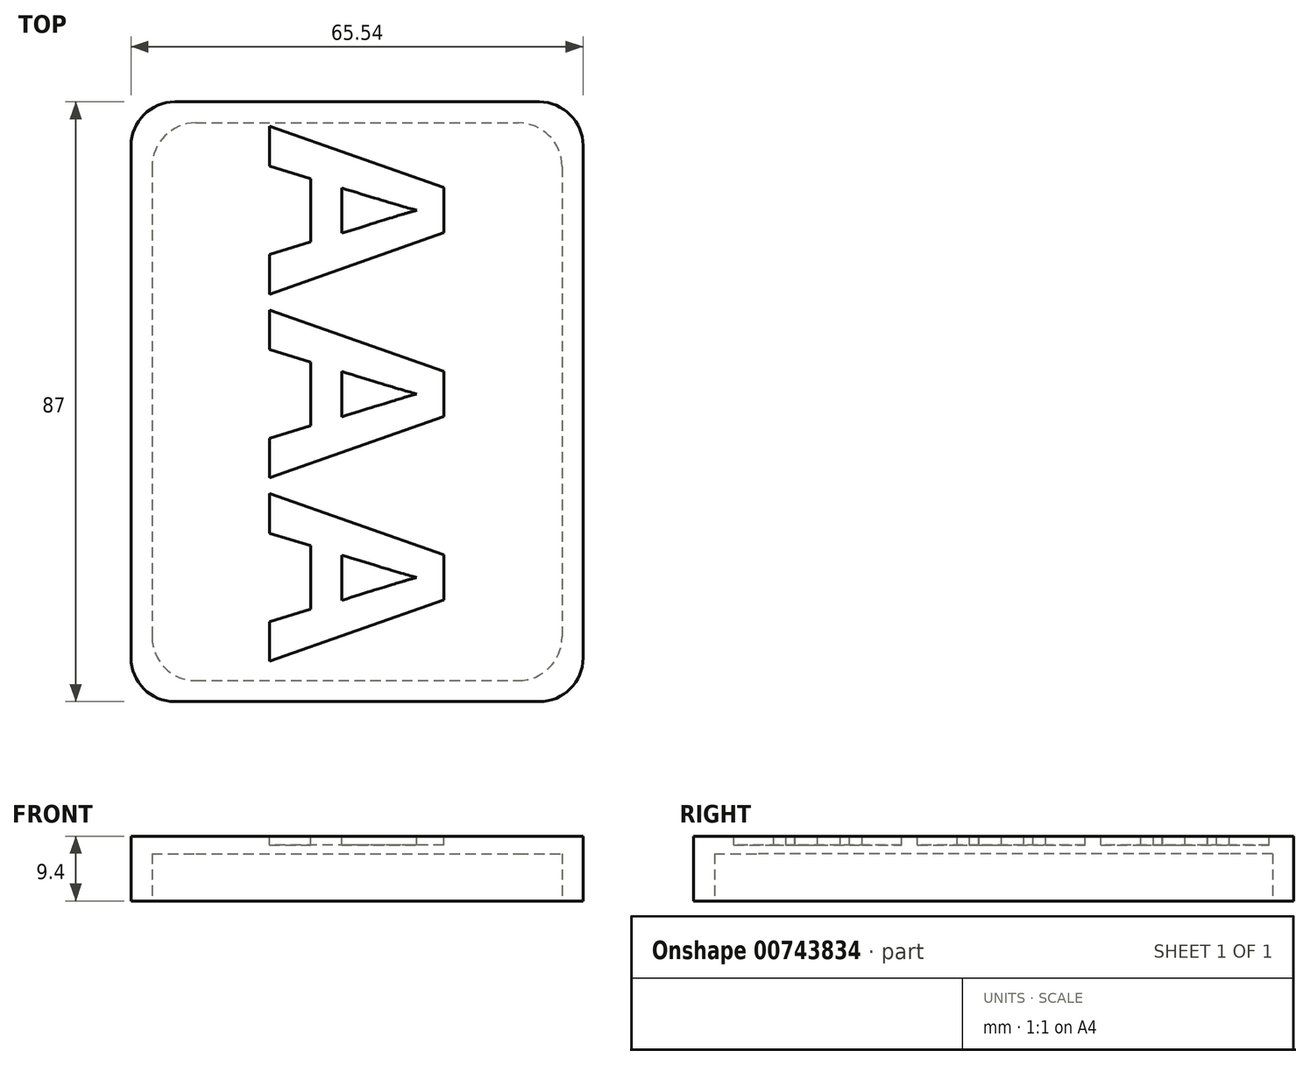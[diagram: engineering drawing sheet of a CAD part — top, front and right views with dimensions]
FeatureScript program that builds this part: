
annotation { "Feature Type Name" : "Feature", "Feature Type Description" : "" }
export const myFeature = defineFeature(function(context is Context, id is Id, definition is map)
    precondition{}
    {
        {
            var Q0;
            Q0=qCreatedBy(makeId("Top.planeOp"),FACE);
            var sketch = newSketch(context, id + "F0", { "sketchPlane" : qUnion([Q0])});
            skLineSegment(sketch, "E0.bottom", {"start": v(-32.77, 43.5) * mm, "end": v(32.77, 43.5) * mm});
            skLineSegment(sketch, "E0.top", {"start": v(-32.77, -43.5) * mm, "end": v(32.77, -43.5) * mm});
            skLineSegment(sketch, "E0.left", {"start": v(-32.77, 43.5) * mm, "end": v(-32.77, -43.5) * mm});
            skLineSegment(sketch, "E0.right", {"start": v(32.77, 43.5) * mm, "end": v(32.77, -43.5) * mm});
            skLineSegment(sketch, "E1", {"start": v(0, 43.5) * mm, "end": v(0, 0) * mm, "construction": true});
            skLineSegment(sketch, "E2", {"start": v(0, 0) * mm, "end": v(-32.77, 0) * mm, "construction": true});
            skSolve(sketch);
        }
        {
            var Q0;
            Q0=qSketchRegion(id+"F0",true);
            extrude(context, id + "F1", {"entities" : qUnion([Q0]), "depth" : 41.27 * mm, "offsetDistance" : 25.4 * mm});
        }
        {
            var Q0;
            Q0=makeQuery(id+"F1.opExtrude","CAP_FACE",FACE,{"disambiguationData":[OSD([sQuery(id+"F0.wireOp",EDGE,"E0.bottom"),sQuery(id+"F0.wireOp",EDGE,"E0.top"),sQuery(id+"F0.wireOp",EDGE,"E0.left"),sQuery(id+"F0.wireOp",EDGE,"E0.right")])],"isStart":false});
            var sketch = newSketch(context, id + "F2", { "sketchPlane" : qUnion([Q0])});
            skCircle(sketch, "E3", {"center": v(-24.2, 34.92) * mm, "radius": 5.4 * mm});
            skCircle(sketch, "E4.1.0.0", {"center": v(-24.2, 20.95) * mm, "radius": 5.4 * mm});
            skCircle(sketch, "E4.2.0.0", {"center": v(-24.2, 6.98) * mm, "radius": 5.4 * mm});
            skLineSegment(sketch, "E4.direction1", {"start": v(-24.2, 34.92) * mm, "end": v(-24.2, 20.95) * mm, "construction": true});
            skCircle(sketch, "E5.0.3.0", {"center": v(-24.2, -6.99) * mm, "radius": 5.4 * mm});
            skCircle(sketch, "E5.0.4.0", {"center": v(-24.2, -20.96) * mm, "radius": 5.4 * mm});
            skCircle(sketch, "E6.0.5.0", {"center": v(-24.2, -34.93) * mm, "radius": 5.4 * mm});
            skCircle(sketch, "E7", {"center": v(-12.1, 27.94) * mm, "radius": 5.4 * mm});
            skLineSegment(sketch, "E8", {"start": v(-12.1, 27.94) * mm, "end": v(-24.2, 34.93) * mm, "construction": true});
            skLineSegment(sketch, "E9", {"start": v(-24.2, 20.95) * mm, "end": v(-12.1, 27.94) * mm, "construction": true});
            skCircle(sketch, "E10.1.0.0", {"center": v(-12.1, 13.97) * mm, "radius": 5.4 * mm});
            skCircle(sketch, "E10.2.0.0", {"center": v(-12.1, 0) * mm, "radius": 5.4 * mm});
            skLineSegment(sketch, "E10.direction1", {"start": v(-12.1, 27.94) * mm, "end": v(-12.1, 13.97) * mm, "construction": true});
            skCircle(sketch, "E11.0.3.0", {"center": v(-12.1, -13.97) * mm, "radius": 5.4 * mm});
            skCircle(sketch, "E11.0.4.0", {"center": v(-12.1, -27.94) * mm, "radius": 5.4 * mm});
            skLineSegment(sketch, "E12.1.0.0", {"start": v(12.1, 27.94) * mm, "end": v(12.1, 13.97) * mm, "construction": true});
            skCircle(sketch, "E12.1.0.1", {"center": v(12.1, 0) * mm, "radius": 5.4 * mm});
            skLineSegment(sketch, "E12.1.0.2", {"start": v(0, 34.92) * mm, "end": v(0, 20.95) * mm, "construction": true});
            skCircle(sketch, "E12.1.0.3", {"center": v(12.1, 13.97) * mm, "radius": 5.4 * mm});
            skLineSegment(sketch, "E12.1.0.4", {"start": v(0, 20.95) * mm, "end": v(12.1, 27.94) * mm, "construction": true});
            skCircle(sketch, "E12.1.0.5", {"center": v(12.1, -13.97) * mm, "radius": 5.4 * mm});
            skCircle(sketch, "E12.1.0.6", {"center": v(0, 6.98) * mm, "radius": 5.4 * mm});
            skCircle(sketch, "E12.1.0.7", {"center": v(0, 20.95) * mm, "radius": 5.4 * mm});
            skCircle(sketch, "E12.1.0.8", {"center": v(0, 34.92) * mm, "radius": 5.4 * mm});
            skCircle(sketch, "E12.1.0.9", {"center": v(12.1, -27.94) * mm, "radius": 5.4 * mm});
            skLineSegment(sketch, "E12.1.0.10", {"start": v(12.1, 27.94) * mm, "end": v(0, 34.93) * mm, "construction": true});
            skCircle(sketch, "E12.1.0.11", {"center": v(12.1, 27.94) * mm, "radius": 5.4 * mm});
            skCircle(sketch, "E12.1.0.12", {"center": v(0, -6.99) * mm, "radius": 5.4 * mm});
            skCircle(sketch, "E12.1.0.13", {"center": v(0, -20.96) * mm, "radius": 5.4 * mm});
            skCircle(sketch, "E12.1.0.14", {"center": v(0, -34.93) * mm, "radius": 5.4 * mm});
            skLineSegment(sketch, "E12.2.0.2", {"start": v(24.2, 34.92) * mm, "end": v(24.2, 20.95) * mm, "construction": true});
            skCircle(sketch, "E12.2.0.6", {"center": v(24.2, 6.98) * mm, "radius": 5.4 * mm});
            skCircle(sketch, "E12.2.0.7", {"center": v(24.2, 20.95) * mm, "radius": 5.4 * mm});
            skCircle(sketch, "E12.2.0.8", {"center": v(24.2, 34.92) * mm, "radius": 5.4 * mm});
            skLineSegment(sketch, "E12.2.0.10", {"start": v(36.3, 27.94) * mm, "end": v(24.2, 34.93) * mm, "construction": true});
            skCircle(sketch, "E12.2.0.12", {"center": v(24.2, -6.99) * mm, "radius": 5.4 * mm});
            skCircle(sketch, "E12.2.0.13", {"center": v(24.2, -20.96) * mm, "radius": 5.4 * mm});
            skCircle(sketch, "E12.2.0.14", {"center": v(24.2, -34.93) * mm, "radius": 5.4 * mm});
            skLineSegment(sketch, "E12.direction1", {"start": v(-24.2, -34.93) * mm, "end": v(0, -34.93) * mm, "construction": true});
            skSolve(sketch);
        }
        {
            var Q0;
            Q0=qSketchRegion(id+"F2",true);
            extrude(context, id + "F3", {"entities" : qUnion([Q0]), "operationType" : NewBodyOperationType.REMOVE, "oppositeDirection" : true, "depth" : 38.1 * mm, "offsetDistance" : 25.4 * mm});
        }
        {
            var Q0;
            Q0=makeQuery(id+"F1.opExtrude","SWEPT_EDGE",EDGE,{"disambiguationData":[OSD([sQuery(id+"F0.wireOp",EDGE,"E0.top"),sQuery(id+"F0.wireOp",EDGE,"E0.left")])]});
            var Q1;
            Q1=makeQuery(id+"F1.opExtrude","SWEPT_EDGE",EDGE,{"disambiguationData":[OSD([sQuery(id+"F0.wireOp",EDGE,"E0.top"),sQuery(id+"F0.wireOp",EDGE,"E0.right")])]});
            var Q2;
            Q2=makeQuery(id+"F1.opExtrude","SWEPT_EDGE",EDGE,{"disambiguationData":[OSD([sQuery(id+"F0.wireOp",EDGE,"E0.bottom"),sQuery(id+"F0.wireOp",EDGE,"E0.right")])]});
            var Q3;
            Q3=makeQuery(id+"F1.opExtrude","SWEPT_EDGE",EDGE,{"disambiguationData":[OSD([sQuery(id+"F0.wireOp",EDGE,"E0.bottom"),sQuery(id+"F0.wireOp",EDGE,"E0.left")])]});
            fillet(context, id + "F4", {"entities" : qUnion([Q0, Q1, Q2, Q3]), "radius" : 6.35 * mm, "tangentPropagation" : true, "allowEdgeOverflow" : false});
        }
        {
            var Q0;
            Q0=makeQuery(id+"F1.opExtrude","CAP_FACE",FACE,{"disambiguationData":[OSD([sQuery(id+"F0.wireOp",EDGE,"E0.bottom"),sQuery(id+"F0.wireOp",EDGE,"E0.top"),sQuery(id+"F0.wireOp",EDGE,"E0.left"),sQuery(id+"F0.wireOp",EDGE,"E0.right")])],"isStart":false});
            var sketch = newSketch(context, id + "F5", { "sketchPlane" : qUnion([Q0])});
            skLineSegment(sketch, "E13.0", {"start": v(-26.42, 43.5) * mm, "end": v(26.42, 43.5) * mm});
            skArc(sketch, "E13.1", {"start": v(32.77, 37.15) * mm, "mid": v(30.9, 41.64) * mm, "end": v(26.42, 43.5) * mm});
            skLineSegment(sketch, "E13.2", {"start": v(32.77, 37.15) * mm, "end": v(32.77, -37.15) * mm});
            skArc(sketch, "E13.3", {"start": v(26.42, -43.5) * mm, "mid": v(30.9, -41.64) * mm, "end": v(32.77, -37.15) * mm});
            skLineSegment(sketch, "E13.4", {"start": v(-26.42, -43.5) * mm, "end": v(26.42, -43.5) * mm});
            skArc(sketch, "E13.5", {"start": v(-32.77, -37.15) * mm, "mid": v(-30.9, -41.64) * mm, "end": v(-26.42, -43.5) * mm});
            skLineSegment(sketch, "E13.6", {"start": v(-32.77, 37.15) * mm, "end": v(-32.77, -37.15) * mm});
            skArc(sketch, "E13.7", {"start": v(-26.42, 43.5) * mm, "mid": v(-30.9, 41.64) * mm, "end": v(-32.77, 37.15) * mm});
            skLineSegment(sketch, "E14.0", {"start": v(29.72, 34.1) * mm, "end": v(29.72, -34.1) * mm});
            skLineSegment(sketch, "E14.1", {"start": v(-23.37, 40.45) * mm, "end": v(23.37, 40.45) * mm});
            skLineSegment(sketch, "E14.2", {"start": v(-29.72, 34.1) * mm, "end": v(-29.72, -34.1) * mm});
            skLineSegment(sketch, "E14.3", {"start": v(-23.37, -40.45) * mm, "end": v(23.37, -40.45) * mm});
            skPoint(sketch, "E15.visualSharp", {"position": v(29.72, -40.45) * mm});
            skArc(sketch, "E15.filletArc", {"start": v(23.37, -40.45) * mm, "mid": v(27.86, -38.59) * mm, "end": v(29.72, -34.1) * mm});
            skPoint(sketch, "E16.visualSharp", {"position": v(-29.72, -40.45) * mm});
            skArc(sketch, "E16.filletArc", {"start": v(-29.72, -34.1) * mm, "mid": v(-27.86, -38.59) * mm, "end": v(-23.37, -40.45) * mm});
            skPoint(sketch, "E17.visualSharp", {"position": v(-29.72, 40.45) * mm});
            skArc(sketch, "E17.filletArc", {"start": v(-23.37, 40.45) * mm, "mid": v(-27.86, 38.59) * mm, "end": v(-29.72, 34.1) * mm});
            skPoint(sketch, "E18.visualSharp", {"position": v(29.72, 40.45) * mm});
            skArc(sketch, "E18.filletArc", {"start": v(29.72, 34.1) * mm, "mid": v(27.86, 38.59) * mm, "end": v(23.37, 40.45) * mm});
            skSolve(sketch);
        }
        {
            var Q0;
            Q0 = qSketchRegion(id + "F5", true);
            extrude(context, id + "F6", {"entities" : qUnion([Q0]), "depth" : 6.86 * mm, "offsetDistance" : 25.4 * mm});
        }
        {
            var Q0;
            Q0=makeQuery(id+"F6.opExtrude","CAP_FACE",FACE,{"disambiguationData":[OSD([sQuery(id+"F5.wireOp",EDGE,"E13.0"),sQuery(id+"F5.wireOp",EDGE,"E13.1"),sQuery(id+"F5.wireOp",EDGE,"E13.2"),sQuery(id+"F5.wireOp",EDGE,"E13.3"),sQuery(id+"F5.wireOp",EDGE,"E13.4"),sQuery(id+"F5.wireOp",EDGE,"E13.5"),sQuery(id+"F5.wireOp",EDGE,"E13.6"),sQuery(id+"F5.wireOp",EDGE,"E13.7"),sQuery(id+"F5.wireOp",EDGE,"E14.0"),sQuery(id+"F5.wireOp",EDGE,"E14.1"),sQuery(id+"F5.wireOp",EDGE,"E14.2"),sQuery(id+"F5.wireOp",EDGE,"E14.3"),sQuery(id+"F5.wireOp",EDGE,"E15.filletArc"),sQuery(id+"F5.wireOp",EDGE,"E16.filletArc"),sQuery(id+"F5.wireOp",EDGE,"E17.filletArc"),sQuery(id+"F5.wireOp",EDGE,"E18.filletArc")])],"isStart":false});
            var sketch = newSketch(context, id + "F7", { "sketchPlane" : qUnion([Q0])});
            skLineSegment(sketch, "E19.0", {"start": v(-32.77, 37.15) * mm, "end": v(-32.77, -37.15) * mm});
            skArc(sketch, "E19.1", {"start": v(-32.77, -37.15) * mm, "mid": v(-30.9, -41.64) * mm, "end": v(-26.42, -43.5) * mm});
            skLineSegment(sketch, "E19.2", {"start": v(-26.42, -43.5) * mm, "end": v(26.42, -43.5) * mm});
            skArc(sketch, "E19.3", {"start": v(26.42, -43.5) * mm, "mid": v(30.9, -41.64) * mm, "end": v(32.77, -37.15) * mm});
            skLineSegment(sketch, "E19.4", {"start": v(32.77, 37.15) * mm, "end": v(32.77, -37.15) * mm});
            skArc(sketch, "E19.5", {"start": v(32.77, 37.15) * mm, "mid": v(30.9, 41.64) * mm, "end": v(26.42, 43.5) * mm});
            skLineSegment(sketch, "E19.6", {"start": v(-26.42, 43.5) * mm, "end": v(26.42, 43.5) * mm});
            skArc(sketch, "E19.7", {"start": v(-26.42, 43.5) * mm, "mid": v(-30.9, 41.64) * mm, "end": v(-32.77, 37.15) * mm});
            skSolve(sketch);
        }
        {
            var Q0;
            Q0 = qSketchRegion(id + "F7", true);
            extrude(context, id + "F8", {"entities" : qUnion([Q0]), "operationType" : NewBodyOperationType.ADD, "depth" : 2.54 * mm, "offsetDistance" : 25.4 * mm});
        }
        {
            var Q0;
            Q0=makeQuery(id+"F1.opExtrude","SWEPT_BODY",BODY,{"disambiguationData":[OSD([sQuery(id+"F0.wireOp",EDGE,"E0.bottom"),sQuery(id+"F0.wireOp",EDGE,"E0.top"),sQuery(id+"F0.wireOp",EDGE,"E0.left"),sQuery(id+"F0.wireOp",EDGE,"E0.right")])]});
            deleteBodies(context, id + "F9", {"entities" : qUnion([Q0])});
        }
        {
            var Q0;
            Q0=makeQuery(id+"F8.opExtrude","CAP_FACE",FACE,{"disambiguationData":[OSD([sQuery(id+"F7.wireOp",EDGE,"E19.0"),sQuery(id+"F7.wireOp",EDGE,"E19.1"),sQuery(id+"F7.wireOp",EDGE,"E19.2"),sQuery(id+"F7.wireOp",EDGE,"E19.3"),sQuery(id+"F7.wireOp",EDGE,"E19.4"),sQuery(id+"F7.wireOp",EDGE,"E19.5"),sQuery(id+"F7.wireOp",EDGE,"E19.6"),sQuery(id+"F7.wireOp",EDGE,"E19.7")])],"isStart":false});
            var sketch = newSketch(context, id + "F10", { "sketchPlane" : qUnion([Q0])});
            skText(sketch, "E20", { "text": "A", "fontName": "OpenSans-Bold.ttf"});
            skText(sketch, "E21", { "text": "A", "fontName": "OpenSans-Bold.ttf"});
            skText(sketch, "E22", { "text": "A", "fontName": "OpenSans-Bold.ttf"});
            const initialGuessF10  = {"E20": [-0.0127, 0.01331, 0, -1, 0.0254], "E21": [-0.0127, -0.01331, 0, -1, 0.0254], "E22": [-0.0127, 0.03994, 0, -1, 0.0254]};
            skSetInitialGuess(sketch, initialGuessF10);
            skSolve(sketch);
        }
        {
            var Q0;
            Q0=makeQuery(id+"F10.imprint","IMPRINT",FACE,{"disambiguationData":[TD([[makeQuery(id+"F10.imprint","IMPRINT",EDGE,{"derivedFrom":sQuery(id+"F10.wireOp",EDGE,"E22.sketch_text.stroke-0")}),-1.0]])]});
            var Q1;
            Q1=makeQuery(id+"F10.imprint","IMPRINT",FACE,{"disambiguationData":[TD([[makeQuery(id+"F10.imprint","IMPRINT",EDGE,{"derivedFrom":sQuery(id+"F10.wireOp",EDGE,"E20.sketch_text.stroke-0")}),-1.0]])]});
            var Q2;
            Q2=makeQuery(id+"F10.imprint","IMPRINT",FACE,{"disambiguationData":[TD([[makeQuery(id+"F10.imprint","IMPRINT",EDGE,{"derivedFrom":sQuery(id+"F10.wireOp",EDGE,"E21.sketch_text.stroke-0")}),-1.0]])]});
            extrude(context, id + "F11", {"entities" : qUnion([Q0, Q1, Q2]), "operationType" : NewBodyOperationType.REMOVE, "oppositeDirection" : true, "depth" : 1.27 * mm, "offsetDistance" : 25.4 * mm});
        }
    });
